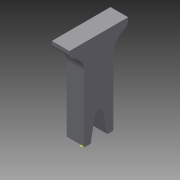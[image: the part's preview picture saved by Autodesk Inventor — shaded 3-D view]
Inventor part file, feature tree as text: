
AUTODESK INVENTOR PART (.ipt)
format: ipt  version: 2015 (Build 190159000, 159)  size: 114,176 bytes
history: native  units: mm
features: extrude x1, sketch x1
ambient origin geometry x8: Origin, YZ Plane, XZ Plane, XY Plane, X Axis, Y Axis, Z Axis, Center Point
bodies: Body1 (feature_tree)
feature tree (2):
  extrude  "Extrusion7"  Depth=10.0mm
  sketch  "Sketch1"  dims[d8=22.5deg d16=3.0mm d25=10.0mm d32=6.0mm d33=6.0mm d70=38.0mm d74=22.5deg d77=3.0mm d81=90.0mm d82=46.0mm d88=20.0mm d90=2.0mm d94=1.0mm d96=22.5deg d107=6.0mm d108=0.0mm d113=12.0mm d114=1.745329mm d115=5.0mm d116=0.5mm d118=36.0mm]
